# Revit family: SINK-U~2
name_source: partatom
category: Plumbing Fixtures
units: mm (PartAtom-declared; Revit-internal decimal feet)

## family parameters
Cut with Voids When Loaded = No
Host = Face
OmniClass Number = 23.31.13.00
Part Type = Normal
Room Calculation Point = No
Round Connector Dimension = Use Diameter
Shared = No

## types (1)
- NA-Stainless
    ADA Compliant = No
    Assembly Code = D2010400
    CW Connection = No
    Colander = Yes
    Cold Water Inlet = Cold Water Inlet
    Cutting Board = Yes
    Date Modified = 11/28/2023
    Default Elevation = 36"
    Description = Single Bowl ADA Sink
    Drain Included = No
    Drying Rack = Yes
    Finish = Kohler-Metal-NA-Stainless
    HW Connection = No
    Height = 6 1/8"
    Hot Water Inlet = Hot Water Inlet
    Length = 29"
    Manufacturer = Kohler Co.
    Master Format 2014 = 22 41 16
    Master Format 2014 Name = Residential Lavatories and Sinks
    Material = Stainless Steel
    Model = K-33661-PC-NA
    Product Documentation Link = https://www.us.kohler.com
    Product Name = Strive
    Product Page URL = http://www.us.kohler.com
    Soaking Bin = Yes
    Type = 1
    URL = https://www.us.kohler.com
    Vent Connection = No
    Waste Connection = Yes
    Waste Water Outlet = Waste Water Outlet
    WaterSense Certified = No
    Width = 18 5/16"

## geometry (parser evidence)
native form markers: Sweep x15
no freeform markers — native parametric forms only
